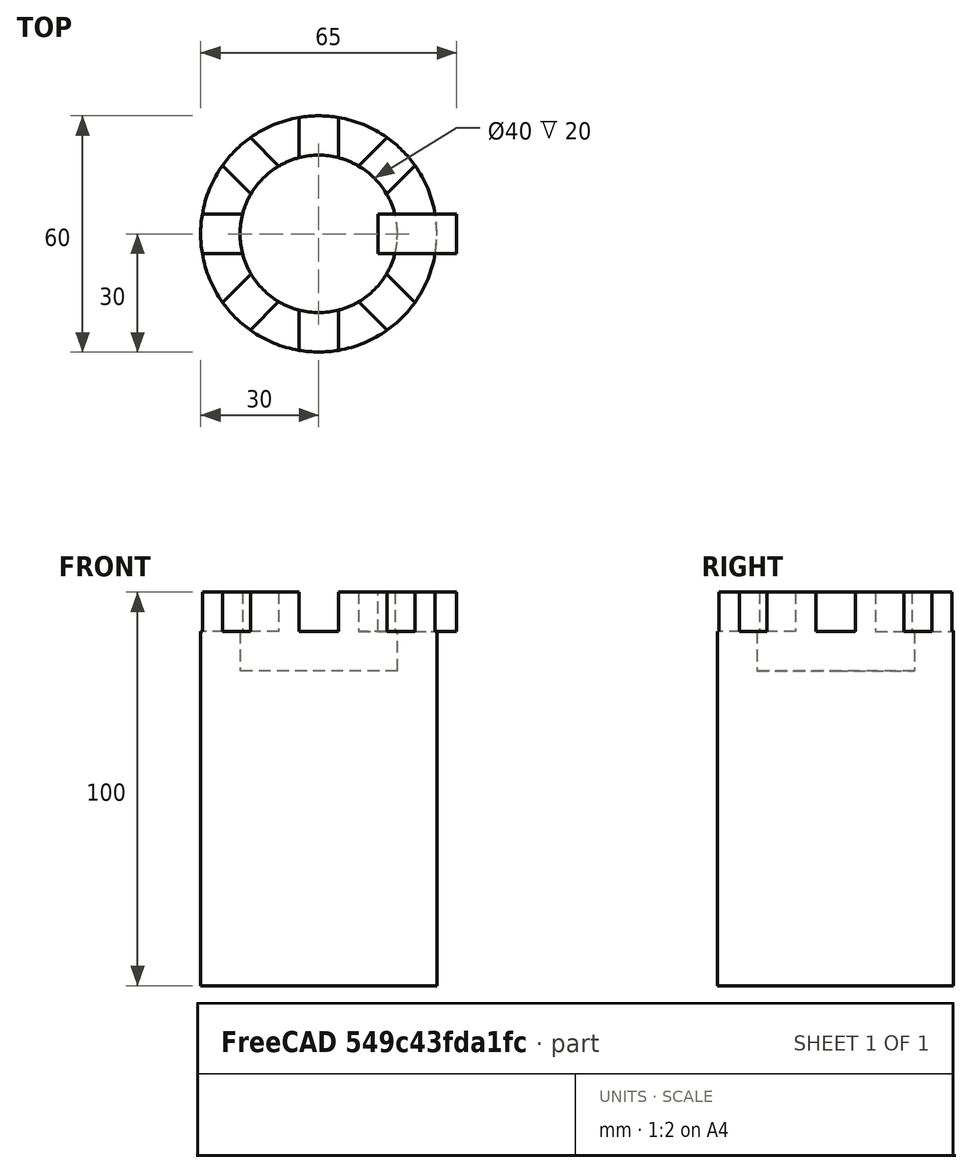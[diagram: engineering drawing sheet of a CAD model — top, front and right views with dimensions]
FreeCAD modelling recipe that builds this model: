
FCSTD DOCUMENT  (FreeCAD 1.0R39285 (Git))
Label: ojt1_t11r03_tower
License: All rights reserved
objects: Part::Cylinder×2, Part::Cut×2, Part::Box×1, Part::FeaturePython×1
note: 5 computed .brp shape members not serialized (recipe doc carries the construction recipe); baked Part::Feature solids carry a one-line shape summary decoded from their .brp

FEATURE [Part::Cylinder] Cylinder  label="Cilindre"
  Angle = 360
  AttacherType = Attacher::AttachEngine3D
  FirstAngle = 0
  Height = 100
  Radius = 30
  SecondAngle = 0
FEATURE [Part::Cylinder] Cylinder001  label="Cilindre001"
  Angle = 360
  AttacherType = Attacher::AttachEngine3D
  FirstAngle = 0
  Height = 50
  Placement = pos=(0,0,80) rot=(0,0,1;0rad)
  Radius = 20
  SecondAngle = 0
FEATURE [Part::Cut] Cut
  Base = -> Cylinder
  Refine = true
  Tool = -> Cylinder001
FEATURE [Part::Box] Box  label="Cub"
  AttacherType = Attacher::AttachEngine3D
  Height = 10
  Length = 20
  Placement = pos=(15,-5,90) rot=(0,0,1;0rad)
  Width = 10
FEATURE [Part::FeaturePython] Array  label="battelment"  # Draft array (typed FeaturePython)
  AlwaysSyncPlacement = false
  Angle = 360
  ArrayType = 1
  Axis = (0,0,1)
  Base = -> Box
  Center = (0,0,1)
  Count = 8
  ExpandArray = false
  Fuse = false
  IntervalAxis = (0,0,0)
  IntervalX = (50,0,0)
  IntervalY = (0,50,0)
  IntervalZ = (0,0,50)
  NumberCircles = 3
  NumberPolar = 8
  NumberX = 2
  NumberY = 2
  NumberZ = 1
  PlacementList = 8 placements: [(15,-5,90),(14.1421,7.07107,90),(5,15,90),(-7.07107,14.1421,90),(-15,5,90),(-14.1421,-7.07107,90),(-5,-15,90),(7.07107,-14.1421,90)]
  RadialDistance = 50
  ScaleList = (8) [(1,1,1),(1,1,1),(1,1,1),(1,1,1),(1,1,1),(1,1,1),(1,1,1),(1,1,1)]
  Symmetry = 1
  TangentialDistance = 25
FEATURE [Part::Cut] Cut001  label="tower"
  Base = -> Cut
  Refine = true
  Tool = -> Array
